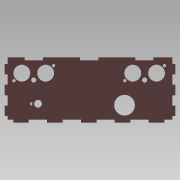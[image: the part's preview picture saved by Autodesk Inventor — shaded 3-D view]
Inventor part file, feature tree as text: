
AUTODESK INVENTOR PART (.ipt)
format: ipt  version: 2015 SP1 (Build 190203100, 203)  size: 186,368 bytes
history: native  units: mm
features: extrude x1, sketch x1
ambient origin geometry x8: Origin, YZ Plane, XZ Plane, XY Plane, X Axis, Y Axis, Z Axis, Center Point
bodies: Body1 (feature_tree)
feature tree (2):
  extrude  "Extrusion2"  Depth=3.0mm
  sketch  "Sketch1"  dims[d4=15.0mm d5=3.0mm d8=30.0mm d10=32.5mm d11=30.0mm d13=32.5mm d16=1.5mm d17=3.0mm d18=10.0mm d19=20.0mm d21=20.0mm d22=20.0mm d24=20.0mm d29=3.0mm d30=0.0mm]
